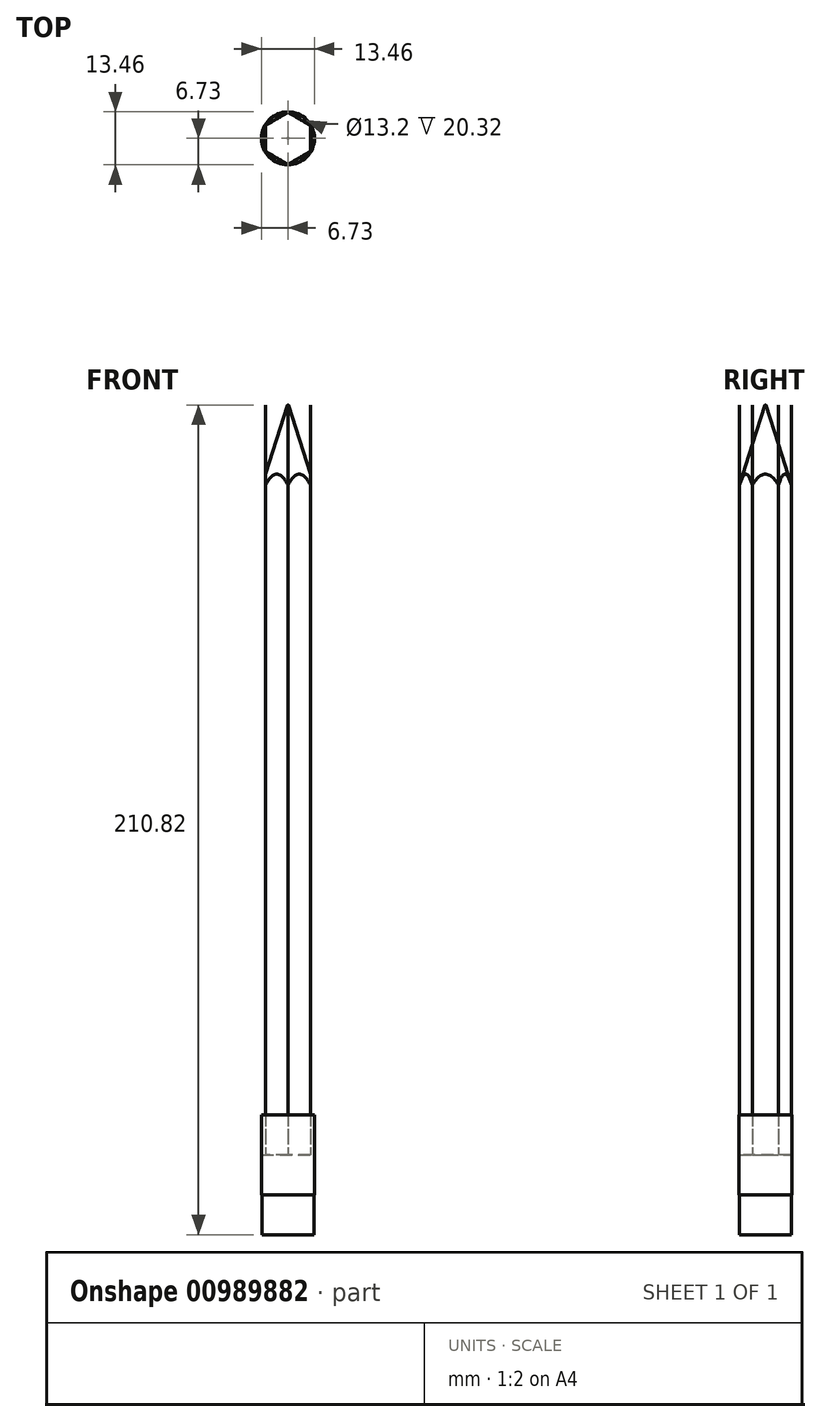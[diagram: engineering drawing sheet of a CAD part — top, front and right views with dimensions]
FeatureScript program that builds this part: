
annotation { "Feature Type Name" : "Feature", "Feature Type Description" : "" }
export const myFeature = defineFeature(function(context is Context, id is Id, definition is map)
    precondition{}
    {
        {
            var Q0;
            Q0=qCreatedBy(makeId("Top.planeOp"),FACE);
            var sketch = newSketch(context, id + "F0", { "sketchPlane" : qUnion([Q0])});
            skCircle(sketch, "E0", {"center": v(0, 0) * mm, "radius": 5.72 * mm});
            skCircle(sketch, "E1.cCircle", {"center": v(0, 0) * mm, "radius": 5.72 * mm, "construction": true});
            skLineSegment(sketch, "E1.0", {"start": v(0, 6.6) * mm, "end": v(5.72, 3.3) * mm});
            skLineSegment(sketch, "E1.1", {"start": v(5.71, 3.3) * mm, "end": v(5.72, -3.3) * mm});
            skLineSegment(sketch, "E1.2", {"start": v(5.72, -3.3) * mm, "end": v(0, -6.6) * mm});
            skLineSegment(sketch, "E1.3", {"start": v(0, -6.6) * mm, "end": v(-5.71, -3.3) * mm});
            skLineSegment(sketch, "E1.4", {"start": v(-5.71, -3.3) * mm, "end": v(-5.72, 3.3) * mm});
            skLineSegment(sketch, "E1.5", {"start": v(-5.72, 3.3) * mm, "end": v(0, 6.6) * mm});
            skPoint(sketch, "E1.0.midPoint", {"position": v(2.86, 4.95) * mm});
            skSolve(sketch);
        }
        {
            var Q0;
            {var subQ0=sQuery(id+"F0.wireOp",EDGE,"E1.5");var subQ1=sQuery(id+"F0.wireOp",EDGE,"E0");var subQ2=makeQuery(id+"F0.imprint","INTERSECT",VERTEX,{"derivedFrom":[subQ1,subQ0]});Q0=makeQuery(id+"F0.imprint","IMPRINT",FACE,{"disambiguationData":[TD([[makeQuery(id+"F0.imprint","IMPRINT",EDGE,{"disambiguationData":[TD([[subQ2,-1.0]])],"derivedFrom":subQ1}),-1.0]])]});}
            var Q1;
            {var subQ0=sQuery(id+"F0.wireOp",EDGE,"E1.0");var subQ1=sQuery(id+"F0.wireOp",EDGE,"E0");var subQ2=makeQuery(id+"F0.imprint","INTERSECT",VERTEX,{"derivedFrom":[subQ1,subQ0]});Q1=makeQuery(id+"F0.imprint","IMPRINT",FACE,{"disambiguationData":[TD([[makeQuery(id+"F0.imprint","IMPRINT",EDGE,{"disambiguationData":[TD([[subQ2,-1.0]])],"derivedFrom":subQ1}),-1.0]])]});}
            var Q2;
            {var subQ0=sQuery(id+"F0.wireOp",EDGE,"E0");var subQ4=makeQuery(id+"F0.imprint","INTERSECT",VERTEX,{"derivedFrom":[subQ0,sQuery(id+"F0.wireOp",EDGE,"E1.0")]});Q2=makeQuery(id+"F0.imprint","IMPRINT",FACE,{"disambiguationData":[TD([[makeQuery(id+"F0.imprint","IMPRINT",EDGE,{"disambiguationData":[TD([[subQ4,1.0]])],"derivedFrom":subQ0}),1.0]])]});}
            var Q3;
            {var subQ0=sQuery(id+"F0.wireOp",EDGE,"E1.0");var subQ1=sQuery(id+"F0.wireOp",EDGE,"E0");var subQ2=makeQuery(id+"F0.imprint","INTERSECT",VERTEX,{"derivedFrom":[subQ1,subQ0]});Q3=makeQuery(id+"F0.imprint","IMPRINT",FACE,{"disambiguationData":[TD([[makeQuery(id+"F0.imprint","IMPRINT",EDGE,{"disambiguationData":[TD([[subQ2,1.0]])],"derivedFrom":subQ1}),-1.0]])]});}
            var Q4;
            {var subQ0=sQuery(id+"F0.wireOp",EDGE,"E1.1");var subQ1=sQuery(id+"F0.wireOp",EDGE,"E0");var subQ2=makeQuery(id+"F0.imprint","INTERSECT",VERTEX,{"derivedFrom":[subQ1,subQ0]});Q4=makeQuery(id+"F0.imprint","IMPRINT",FACE,{"disambiguationData":[TD([[makeQuery(id+"F0.imprint","IMPRINT",EDGE,{"disambiguationData":[TD([[subQ2,1.0]])],"derivedFrom":subQ1}),-1.0]])]});}
            var Q5;
            {var subQ0=sQuery(id+"F0.wireOp",EDGE,"E1.3");var subQ1=sQuery(id+"F0.wireOp",EDGE,"E0");var subQ2=makeQuery(id+"F0.imprint","INTERSECT",VERTEX,{"derivedFrom":[subQ1,subQ0]});Q5=makeQuery(id+"F0.imprint","IMPRINT",FACE,{"disambiguationData":[TD([[makeQuery(id+"F0.imprint","IMPRINT",EDGE,{"disambiguationData":[TD([[subQ2,-1.0]])],"derivedFrom":subQ1}),-1.0]])]});}
            var Q6;
            {var subQ0=sQuery(id+"F0.wireOp",EDGE,"E1.4");var subQ1=sQuery(id+"F0.wireOp",EDGE,"E0");var subQ2=makeQuery(id+"F0.imprint","INTERSECT",VERTEX,{"derivedFrom":[subQ1,subQ0]});Q6=makeQuery(id+"F0.imprint","IMPRINT",FACE,{"disambiguationData":[TD([[makeQuery(id+"F0.imprint","IMPRINT",EDGE,{"disambiguationData":[TD([[subQ2,-1.0]])],"derivedFrom":subQ1}),-1.0]])]});}
            extrude(context, id + "F1", {"entities" : qUnion([Q0, Q1, Q2, Q3, Q4, Q5, Q6]), "depth" : 190.5 * mm, "offsetDistance" : 25.4 * mm});
        }
        {
            var Q0;
            Q0=makeQuery(id+"F1.opExtrude","CAP_FACE",FACE,{"disambiguationData":[OSD([sQuery(id+"F0.wireOp",EDGE,"E1.0"),sQuery(id+"F0.wireOp",EDGE,"E1.1"),sQuery(id+"F0.wireOp",EDGE,"E1.2"),sQuery(id+"F0.wireOp",EDGE,"E1.3"),sQuery(id+"F0.wireOp",EDGE,"E1.4"),sQuery(id+"F0.wireOp",EDGE,"E1.5")])],"isStart":true});
            var sketch = newSketch(context, id + "F2", { "sketchPlane" : qUnion([Q0])});
            skCircle(sketch, "E2", {"center": v(0, 0) * mm, "radius": 6.6 * mm});
            skCircle(sketch, "E3", {"center": v(0, 0) * mm, "radius": 6.73 * mm});
            skSolve(sketch);
        }
        {
            var Q0;
            Q0=makeQuery(id+"F2.imprint","IMPRINT",FACE,{"disambiguationData":[TD([[makeQuery(id+"F2.imprint","IMPRINT",EDGE,{"derivedFrom":sQuery(id+"F2.wireOp",EDGE,"E3")}),1.0]])]});
            extrude(context, id + "F3", {"entities" : qUnion([Q0]), "endBound" : BoundingType.SYMMETRIC, "depth" : 20.32 * mm, "offsetDistance" : 25.4 * mm});
        }
        {
            var Q0;
            Q0=makeQuery(id+"F1.opExtrude","CAP_FACE",FACE,{"disambiguationData":[OSD([sQuery(id+"F0.wireOp",EDGE,"E1.0"),sQuery(id+"F0.wireOp",EDGE,"E1.1"),sQuery(id+"F0.wireOp",EDGE,"E1.2"),sQuery(id+"F0.wireOp",EDGE,"E1.3"),sQuery(id+"F0.wireOp",EDGE,"E1.4"),sQuery(id+"F0.wireOp",EDGE,"E1.5")])],"isStart":true});
            var sketch = newSketch(context, id + "F4", { "sketchPlane" : qUnion([Q0])});
            skCircle(sketch, "E4", {"center": v(0, 0) * mm, "radius": 6.6 * mm});
            skSolve(sketch);
        }
        {
            var Q0;
            Q0 = qSketchRegion(id + "F4", true);
            extrude(context, id + "F5", {"entities" : qUnion([Q0]), "depth" : 20.32 * mm, "offsetDistance" : 25.4 * mm});
        }
        {
            var Q0;
            Q0=makeQuery(id+"F1.opExtrude","CAP_FACE",FACE,{"disambiguationData":[OSD([sQuery(id+"F0.wireOp",EDGE,"E1.0"),sQuery(id+"F0.wireOp",EDGE,"E1.1"),sQuery(id+"F0.wireOp",EDGE,"E1.2"),sQuery(id+"F0.wireOp",EDGE,"E1.3"),sQuery(id+"F0.wireOp",EDGE,"E1.4"),sQuery(id+"F0.wireOp",EDGE,"E1.5")])],"isStart":false});
            var sketch = newSketch(context, id + "F6", { "sketchPlane" : qUnion([Q0])});
            skCircle(sketch, "E5", {"center": v(0, 0) * mm, "radius": 6.6 * mm, "construction": true});
            skSolve(sketch);
        }
        {
            var Q0;
            Q0=qCreatedBy(makeId("Front.planeOp"),FACE);
            var sketch = newSketch(context, id + "F7", { "sketchPlane" : qUnion([Q0])});
            skLineSegment(sketch, "E6", {"start": v(0.1, 190.5) * mm, "end": v(6.6, 170.18) * mm});
            skLineSegment(sketch, "E7", {"start": v(0.1, 190.5) * mm, "end": v(6.6, 190.5) * mm});
            skLineSegment(sketch, "E8", {"start": v(0, 190.5) * mm, "end": v(5.7, 190.5) * mm, "construction": true});
            skLineSegment(sketch, "E9", {"start": v(6.6, 190.5) * mm, "end": v(6.6, 170.18) * mm});
            skSolve(sketch);
        }
        {
            var Q0;
            Q0=qCreatedBy(makeId("Front.planeOp"),FACE);
            var sketch = newSketch(context, id + "F8", { "sketchPlane" : qUnion([Q0])});
            skLineSegment(sketch, "E10", {"start": v(0, 0) * mm, "end": v(0, 190.5) * mm, "construction": true});
            skSolve(sketch);
        }
        {
            var Q0;
            Q0 = qSketchRegion(id + "F7", true);
            var Q1;
            Q1=sQuery(id+"F8.wireOp",EDGE,"E10");
            revolve(context, id + "F9", {"operationType" : NewBodyOperationType.REMOVE, "surfaceOperationType" : NewSurfaceOperationType.NEW, "entities" : qUnion([Q0]), "axis" : qUnion([Q1]), "revolveType" : RevolveType.FULL, "oppositeDirection" : true});
        }
    });
